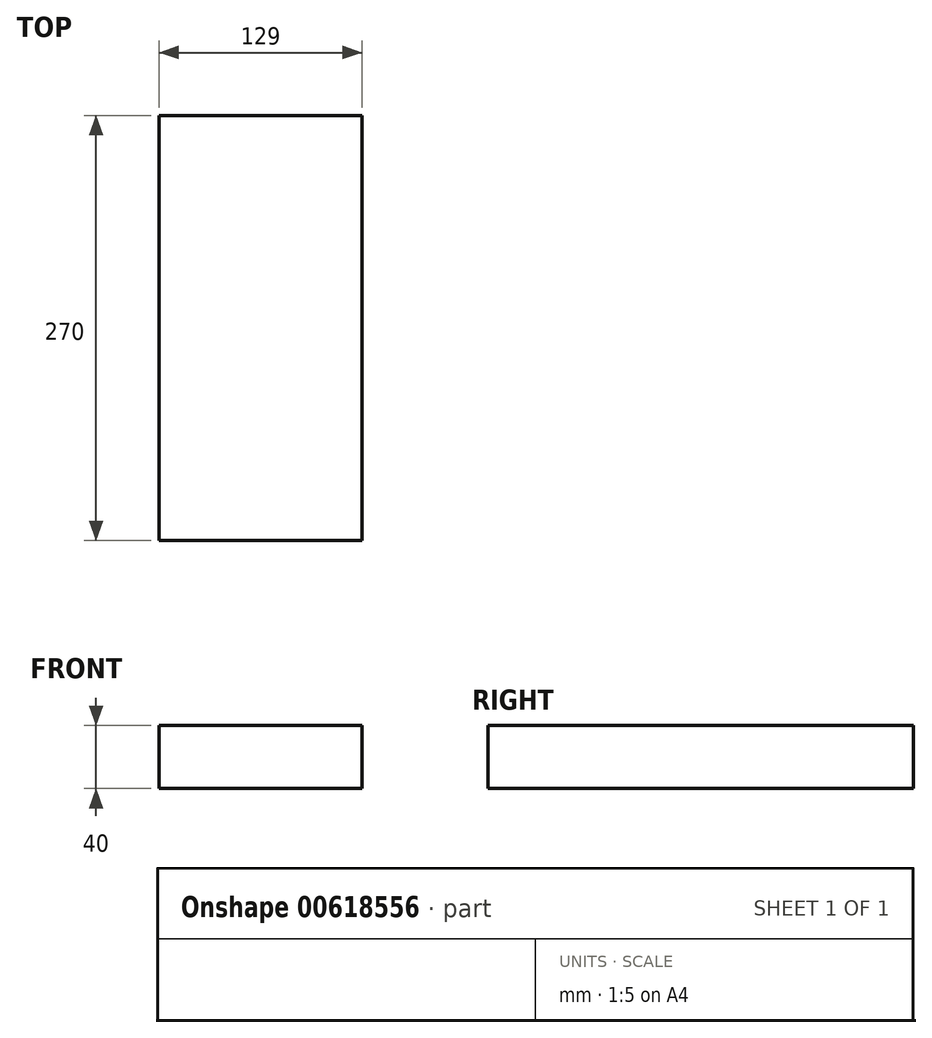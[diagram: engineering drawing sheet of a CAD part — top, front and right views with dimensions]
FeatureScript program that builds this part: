
annotation { "Feature Type Name" : "Feature", "Feature Type Description" : "" }
export const myFeature = defineFeature(function(context is Context, id is Id, definition is map)
    precondition{}
    {
        {
            var Q0;
            Q0=qCreatedBy(makeId("Top.planeOp"),FACE);
            var sketch = newSketch(context, id + "F0", { "sketchPlane" : qUnion([Q0])});
            skLineSegment(sketch, "E0.bottom", {"start": v(64.5, 135) * mm, "end": v(-64.5, 135) * mm});
            skLineSegment(sketch, "E0.top", {"start": v(64.5, -135) * mm, "end": v(-64.5, -135) * mm});
            skLineSegment(sketch, "E0.left", {"start": v(64.5, 135) * mm, "end": v(64.5, -135) * mm});
            skLineSegment(sketch, "E0.right", {"start": v(-64.5, 135) * mm, "end": v(-64.5, -135) * mm});
            skPoint(sketch, "E0.middle", {"position": v(0, 0) * mm});
            skSolve(sketch);
        }
        {
            var Q0;
            Q0=makeQuery(id+"F0.imprint","IMPRINT",FACE,{"disambiguationData":[TD([[makeQuery(id+"F0.imprint","IMPRINT",EDGE,{"derivedFrom":sQuery(id+"F0.wireOp",EDGE,"E0.bottom")}),1.0]])]});
            extrude(context, id + "F1", {"entities" : qUnion([Q0]), "oppositeDirection" : true, "depth" : 40 * mm, "offsetDistance" : 25 * mm});
        }
    });
